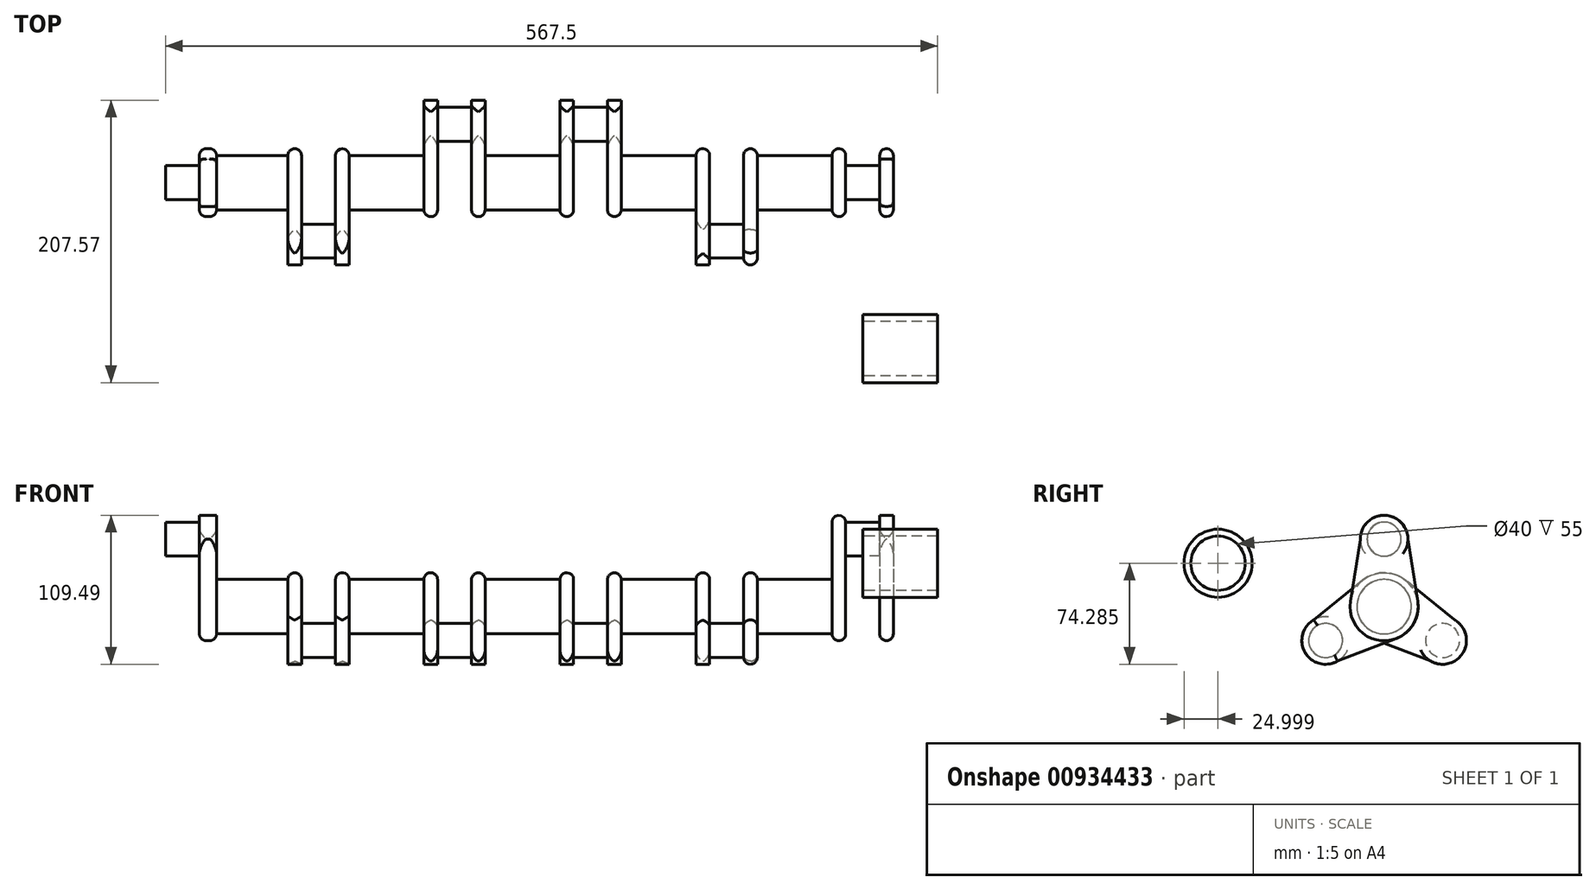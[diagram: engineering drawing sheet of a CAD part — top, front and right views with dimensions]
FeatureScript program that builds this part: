
annotation { "Feature Type Name" : "Feature", "Feature Type Description" : "" }
export const myFeature = defineFeature(function(context is Context, id is Id, definition is map)
    precondition{}
    {
        {
            var Q0;
            Q0=qCreatedBy(makeId("Right.planeOp"),FACE);
            cPlane(context, id + "F0", {"entities" : qUnion([Q0]), "cplaneType" : CPlaneType.OFFSET, "offset" : 100 * mm, "width" : 150 * mm, "height" : 150 * mm});
        }
        {
            var Q0;
            Q0=qCreatedBy(id+"F0.planeOp",FACE);
            cPlane(context, id + "F1", {"entities" : qUnion([Q0]), "cplaneType" : CPlaneType.OFFSET, "offset" : 100 * mm, "width" : 150 * mm, "height" : 150 * mm});
        }
        {
            var Q0;
            Q0=qCreatedBy(id+"F1.planeOp",FACE);
            cPlane(context, id + "F2", {"entities" : qUnion([Q0]), "cplaneType" : CPlaneType.OFFSET, "offset" : 100 * mm, "width" : 150 * mm, "height" : 150 * mm});
        }
        {
            var Q0;
            Q0=qCreatedBy(makeId("Right.planeOp"),FACE);
            cPlane(context, id + "F3", {"entities" : qUnion([Q0]), "cplaneType" : CPlaneType.OFFSET, "offset" : 100 * mm, "oppositeDirection" : true, "width" : 150 * mm, "height" : 150 * mm});
        }
        {
            var Q0;
            Q0=qCreatedBy(id+"F3.planeOp",FACE);
            cPlane(context, id + "F4", {"entities" : qUnion([Q0]), "cplaneType" : CPlaneType.OFFSET, "offset" : 100 * mm, "oppositeDirection" : true, "width" : 150 * mm, "height" : 150 * mm});
        }
        {
            var Q0;
            Q0=qCreatedBy(id+"F2.planeOp",FACE);
            var sketch = newSketch(context, id + "F5", { "sketchPlane" : qUnion([Q0])});
            skCircle(sketch, "E0", {"center": v(0, 0) * mm, "radius": 20 * mm});
            skCircle(sketch, "E1", {"center": v(0, 0) * mm, "radius": 49.66 * mm, "construction": true});
            skCircle(sketch, "E2", {"center": v(0, 49.66) * mm, "radius": 12.5 * mm});
            skLineSegment(sketch, "E3", {"start": v(0, 49.66) * mm, "end": v(0, 0) * mm, "construction": true});
            skLineSegment(sketch, "E4", {"start": v(43, -24.83) * mm, "end": v(0, 0) * mm, "construction": true});
            skSolve(sketch);
        }
        {
            var Q0;
            Q0=qCreatedBy(id+"F4.planeOp",FACE);
            var sketch = newSketch(context, id + "F6", { "sketchPlane" : qUnion([Q0])});
            skCircle(sketch, "E5", {"center": v(0, 0) * mm, "radius": 20 * mm});
            skCircle(sketch, "E6", {"center": v(0, 0) * mm, "radius": 49.66 * mm, "construction": true});
            skCircle(sketch, "E7", {"center": v(0, 49.66) * mm, "radius": 12.5 * mm});
            skLineSegment(sketch, "E8", {"start": v(0, 49.66) * mm, "end": v(0, 0) * mm, "construction": true});
            skLineSegment(sketch, "E9", {"start": v(43, -24.83) * mm, "end": v(0, 0) * mm, "construction": true});
            skSolve(sketch);
        }
        {
            var Q0;
            Q0=qCreatedBy(id+"F1.planeOp",FACE);
            var sketch = newSketch(context, id + "F7", { "sketchPlane" : qUnion([Q0])});
            skCircle(sketch, "E10", {"center": v(0, 0) * mm, "radius": 20 * mm});
            skCircle(sketch, "E11", {"center": v(0, 0) * mm, "radius": 49.66 * mm, "construction": true});
            skLineSegment(sketch, "E12", {"start": v(0, 49.66) * mm, "end": v(0, 0) * mm, "construction": true});
            skLineSegment(sketch, "E13", {"start": v(43, -24.83) * mm, "end": v(0, 0) * mm, "construction": true});
            skCircle(sketch, "E14.1.0", {"center": v(-43, -24.83) * mm, "radius": 12.5 * mm});
            skSolve(sketch);
        }
        {
            var Q0;
            Q0=qCreatedBy(id+"F3.planeOp",FACE);
            var sketch = newSketch(context, id + "F8", { "sketchPlane" : qUnion([Q0])});
            skCircle(sketch, "E15", {"center": v(0, 0) * mm, "radius": 20 * mm});
            skCircle(sketch, "E16", {"center": v(0, 0) * mm, "radius": 49.66 * mm, "construction": true});
            skLineSegment(sketch, "E17", {"start": v(0, 49.66) * mm, "end": v(0, 0) * mm, "construction": true});
            skLineSegment(sketch, "E18", {"start": v(43, -24.83) * mm, "end": v(0, 0) * mm, "construction": true});
            skCircle(sketch, "E19.1.0", {"center": v(-43, -24.83) * mm, "radius": 12.5 * mm});
            skSolve(sketch);
        }
        {
            var Q0;
            Q0=qCreatedBy(makeId("Right.planeOp"),FACE);
            var sketch = newSketch(context, id + "F9", { "sketchPlane" : qUnion([Q0])});
            skCircle(sketch, "E20", {"center": v(0, 0) * mm, "radius": 20 * mm});
            skCircle(sketch, "E21", {"center": v(0, 0) * mm, "radius": 49.66 * mm, "construction": true});
            skLineSegment(sketch, "E22", {"start": v(0, 49.66) * mm, "end": v(0, 0) * mm, "construction": true});
            skLineSegment(sketch, "E23", {"start": v(43, -24.83) * mm, "end": v(0, 0) * mm, "construction": true});
            skCircle(sketch, "E24", {"center": v(43, -24.83) * mm, "radius": 12.5 * mm});
            skSolve(sketch);
        }
        {
            var Q0;
            Q0=qCreatedBy(id+"F0.planeOp",FACE);
            var sketch = newSketch(context, id + "F10", { "sketchPlane" : qUnion([Q0])});
            skCircle(sketch, "E25", {"center": v(0, 0) * mm, "radius": 20 * mm});
            skCircle(sketch, "E26", {"center": v(0, 0) * mm, "radius": 49.66 * mm, "construction": true});
            skLineSegment(sketch, "E27", {"start": v(0, 49.66) * mm, "end": v(0, 0) * mm, "construction": true});
            skLineSegment(sketch, "E28", {"start": v(43, -24.83) * mm, "end": v(0, 0) * mm, "construction": true});
            skCircle(sketch, "E29", {"center": v(43, -24.83) * mm, "radius": 12.5 * mm});
            skSolve(sketch);
        }
        {
            var Q0;
            Q0=makeQuery(id+"F6.imprint","IMPRINT",FACE,{"disambiguationData":[TD([[makeQuery(id+"F6.imprint","IMPRINT",EDGE,{"derivedFrom":sQuery(id+"F6.wireOp",EDGE,"E7")}),1.0]])]});
            var Q1;
            Q1=makeQuery(id+"F8.imprint","IMPRINT",FACE,{"disambiguationData":[TD([[makeQuery(id+"F8.imprint","IMPRINT",EDGE,{"derivedFrom":sQuery(id+"F8.wireOp",EDGE,"E19.1.0")}),1.0]])]});
            var Q2;
            Q2=makeQuery(id+"F9.imprint","IMPRINT",FACE,{"disambiguationData":[TD([[makeQuery(id+"F9.imprint","IMPRINT",EDGE,{"derivedFrom":sQuery(id+"F9.wireOp",EDGE,"E24")}),1.0]])]});
            var Q3;
            Q3=makeQuery(id+"F10.imprint","IMPRINT",FACE,{"disambiguationData":[TD([[makeQuery(id+"F10.imprint","IMPRINT",EDGE,{"derivedFrom":sQuery(id+"F10.wireOp",EDGE,"E29")}),1.0]])]});
            var Q4;
            Q4=makeQuery(id+"F7.imprint","IMPRINT",FACE,{"disambiguationData":[TD([[makeQuery(id+"F7.imprint","IMPRINT",EDGE,{"derivedFrom":sQuery(id+"F7.wireOp",EDGE,"E14.1.0")}),1.0]])]});
            var Q5;
            Q5=makeQuery(id+"F5.imprint","IMPRINT",FACE,{"disambiguationData":[TD([[makeQuery(id+"F5.imprint","IMPRINT",EDGE,{"derivedFrom":sQuery(id+"F5.wireOp",EDGE,"E2")}),1.0]])]});
            extrude(context, id + "F11", {"entities" : qUnion([Q0, Q1, Q2, Q3, Q4, Q5]), "endBound" : BoundingType.SYMMETRIC, "depth" : 25 * mm, "offsetDistance" : 25 * mm});
        }
        {
            var Q0;
            Q0=makeQuery(id+"F11.opExtrude","CAP_FACE",FACE,{"disambiguationData":[OSD([sQuery(id+"F6.wireOp",EDGE,"E7")])],"isStart":false});
            var sketch = newSketch(context, id + "F12", { "sketchPlane" : qUnion([Q0])});
            skPoint(sketch, "E30.center.orphan", {"position": v(0, 49.66) * mm});
            skPoint(sketch, "E31.end.orphan", {"position": v(-12.5, 49.66) * mm});
            skArc(sketch, "E32", {"start": v(-24.7, 3.88) * mm, "mid": v(0, -25) * mm, "end": v(24.7, 3.88) * mm});
            skArc(sketch, "E33", {"start": v(17.5, 49.66) * mm, "mid": v(0, 67.16) * mm, "end": v(-17.5, 49.66) * mm});
            skLineSegment(sketch, "E34", {"start": v(-17.5, 49.66) * mm, "end": v(-24.7, 3.88) * mm});
            skLineSegment(sketch, "E35.MirrorCS", {"start": v(17.5, 49.66) * mm, "end": v(24.7, 3.88) * mm});
            skPoint(sketch, "E36.orphan", {"position": v(25.3, 0) * mm});
            skPoint(sketch, "E37.orphan", {"position": v(-25.3, 0) * mm});
            skSolve(sketch);
        }
        {
            var Q0;
            Q0 = qSketchRegion(id + "F12", true);
            extrude(context, id + "F13", {"entities" : qUnion([Q0]), "operationType" : NewBodyOperationType.ADD, "depth" : 12.5 * mm, "offsetDistance" : 25 * mm});
        }
        {
            var Q0;
            Q0=makeQuery(id+"F13.opExtrude","CAP_FACE",FACE,{"disambiguationData":[OSD([sQuery(id+"F12.wireOp",EDGE,"E32"),sQuery(id+"F12.wireOp",EDGE,"E33"),sQuery(id+"F12.wireOp",EDGE,"E34"),sQuery(id+"F12.wireOp",EDGE,"E35.MirrorCS")])],"isStart":false});
            var sketch = newSketch(context, id + "F14", { "sketchPlane" : qUnion([Q0])});
            skCircle(sketch, "E38", {"center": v(0, 0) * mm, "radius": 20 * mm});
            skSolve(sketch);
        }
        {
            var Q0;
            Q0 = qSketchRegion(id + "F14", true);
            extrude(context, id + "F15", {"entities" : qUnion([Q0]), "operationType" : NewBodyOperationType.ADD, "depth" : 53 * mm, "offsetDistance" : 25 * mm});
        }
        {
            var Q0;
            Q0=makeQuery(id+"F11.opExtrude","CAP_FACE",FACE,{"disambiguationData":[OSD([sQuery(id+"F8.wireOp",EDGE,"E19.1.0")])],"isStart":true});
            var sketch = newSketch(context, id + "F16", { "sketchPlane" : qUnion([Q0])});
            skPoint(sketch, "E39.center.orphan", {"position": v(43, -24.83) * mm});
            skPoint(sketch, "E40.end.orphan", {"position": v(49.25, -14) * mm});
            skArc(sketch, "E41", {"start": v(15.71, 19.45) * mm, "mid": v(-21.65, 12.5) * mm, "end": v(-8.99, -23.33) * mm});
            skArc(sketch, "E42", {"start": v(34.25, -39.98) * mm, "mid": v(58.16, -33.58) * mm, "end": v(51.75, -9.67) * mm});
            skLineSegment(sketch, "E43", {"start": v(51.75, -9.67) * mm, "end": v(15.71, 19.45) * mm});
            skLineSegment(sketch, "E44.MirrorCS", {"start": v(34.25, -39.98) * mm, "end": v(-8.99, -23.33) * mm});
            skPoint(sketch, "E45.orphan", {"position": v(-12.65, -21.92) * mm});
            skPoint(sketch, "E46.orphan", {"position": v(12.65, 21.92) * mm});
            skSolve(sketch);
        }
        {
            var Q0;
            Q0 = qSketchRegion(id + "F16", true);
            extrude(context, id + "F17", {"entities" : qUnion([Q0]), "operationType" : NewBodyOperationType.ADD, "depth" : 10 * mm, "offsetDistance" : 25 * mm});
        }
        {
            var Q0;
            Q0=makeQuery(id+"F11.opExtrude","CAP_FACE",FACE,{"disambiguationData":[OSD([sQuery(id+"F8.wireOp",EDGE,"E19.1.0")])],"isStart":false});
            var sketch = newSketch(context, id + "F18", { "sketchPlane" : qUnion([Q0])});
            skPoint(sketch, "E47.center.orphan", {"position": v(-43, -24.83) * mm});
            skPoint(sketch, "E48.end.orphan", {"position": v(-36.75, -35.65) * mm});
            skArc(sketch, "E49", {"start": v(8.99, -23.33) * mm, "mid": v(21.65, 12.5) * mm, "end": v(-15.71, 19.45) * mm});
            skArc(sketch, "E50", {"start": v(-51.75, -9.67) * mm, "mid": v(-58.16, -33.58) * mm, "end": v(-34.25, -39.98) * mm});
            skLineSegment(sketch, "E51", {"start": v(-34.25, -39.98) * mm, "end": v(8.99, -23.33) * mm});
            skLineSegment(sketch, "E52.MirrorCS", {"start": v(-51.75, -9.67) * mm, "end": v(-15.71, 19.45) * mm});
            skPoint(sketch, "E53.orphan", {"position": v(-12.65, 21.92) * mm});
            skPoint(sketch, "E54.orphan", {"position": v(12.65, -21.92) * mm});
            skSolve(sketch);
        }
        {
            var Q0;
            Q0 = qSketchRegion(id + "F18", true);
            extrude(context, id + "F19", {"entities" : qUnion([Q0]), "operationType" : NewBodyOperationType.ADD, "depth" : 10 * mm, "offsetDistance" : 25 * mm});
        }
        {
            var Q0;
            Q0=makeQuery(id+"F11.opExtrude","CAP_FACE",FACE,{"disambiguationData":[OSD([sQuery(id+"F9.wireOp",EDGE,"E24")])],"isStart":true});
            var sketch = newSketch(context, id + "F20", { "sketchPlane" : qUnion([Q0])});
            skPoint(sketch, "E55.center.orphan", {"position": v(-43, -24.83) * mm});
            skPoint(sketch, "E56.end.orphan", {"position": v(-36.75, -35.65) * mm});
            skArc(sketch, "E57", {"start": v(8.99, -23.33) * mm, "mid": v(21.65, 12.5) * mm, "end": v(-15.71, 19.45) * mm});
            skArc(sketch, "E58", {"start": v(-51.75, -9.67) * mm, "mid": v(-58.16, -33.58) * mm, "end": v(-34.25, -39.98) * mm});
            skLineSegment(sketch, "E59", {"start": v(-34.25, -39.98) * mm, "end": v(8.99, -23.33) * mm});
            skLineSegment(sketch, "E60.MirrorCS", {"start": v(-51.75, -9.67) * mm, "end": v(-15.71, 19.45) * mm});
            skPoint(sketch, "E61.orphan", {"position": v(-12.65, 21.92) * mm});
            skPoint(sketch, "E62.orphan", {"position": v(12.65, -21.92) * mm});
            skSolve(sketch);
        }
        {
            var Q0;
            Q0 = qSketchRegion(id + "F20", true);
            extrude(context, id + "F21", {"entities" : qUnion([Q0]), "operationType" : NewBodyOperationType.ADD, "depth" : 10 * mm, "offsetDistance" : 25 * mm});
        }
        {
            var Q0;
            Q0=makeQuery(id+"F11.opExtrude","CAP_FACE",FACE,{"disambiguationData":[OSD([sQuery(id+"F9.wireOp",EDGE,"E24")])],"isStart":false});
            var sketch = newSketch(context, id + "F22", { "sketchPlane" : qUnion([Q0])});
            skPoint(sketch, "E63.center.orphan", {"position": v(43, -24.83) * mm});
            skPoint(sketch, "E64.end.orphan", {"position": v(49.25, -14) * mm});
            skArc(sketch, "E65", {"start": v(15.71, 19.45) * mm, "mid": v(-21.65, 12.5) * mm, "end": v(-8.99, -23.33) * mm});
            skArc(sketch, "E66", {"start": v(34.25, -39.98) * mm, "mid": v(58.16, -33.58) * mm, "end": v(51.75, -9.67) * mm});
            skLineSegment(sketch, "E67", {"start": v(51.75, -9.67) * mm, "end": v(15.71, 19.45) * mm});
            skLineSegment(sketch, "E68.MirrorCS", {"start": v(34.25, -39.98) * mm, "end": v(-8.99, -23.33) * mm});
            skPoint(sketch, "E69.orphan", {"position": v(-12.65, -21.92) * mm});
            skPoint(sketch, "E70.orphan", {"position": v(12.65, 21.92) * mm});
            skSolve(sketch);
        }
        {
            var Q0;
            Q0 = qSketchRegion(id + "F22", true);
            extrude(context, id + "F23", {"entities" : qUnion([Q0]), "operationType" : NewBodyOperationType.ADD, "depth" : 10 * mm, "offsetDistance" : 25 * mm});
        }
        {
            var Q0;
            Q0=makeQuery(id+"F11.opExtrude","CAP_FACE",FACE,{"disambiguationData":[OSD([sQuery(id+"F10.wireOp",EDGE,"E29")])],"isStart":false});
            var sketch = newSketch(context, id + "F24", { "sketchPlane" : qUnion([Q0])});
            skPoint(sketch, "E71.center.orphan", {"position": v(43, -24.83) * mm});
            skPoint(sketch, "E72.end.orphan", {"position": v(49.25, -14) * mm});
            skArc(sketch, "E73", {"start": v(15.71, 19.45) * mm, "mid": v(-21.65, 12.5) * mm, "end": v(-8.99, -23.33) * mm});
            skArc(sketch, "E74", {"start": v(34.25, -39.98) * mm, "mid": v(58.16, -33.58) * mm, "end": v(51.75, -9.67) * mm});
            skLineSegment(sketch, "E75", {"start": v(51.75, -9.67) * mm, "end": v(15.71, 19.45) * mm});
            skLineSegment(sketch, "E76.MirrorCS", {"start": v(34.25, -39.98) * mm, "end": v(-8.99, -23.33) * mm});
            skPoint(sketch, "E77.orphan", {"position": v(-12.65, -21.92) * mm});
            skPoint(sketch, "E78.orphan", {"position": v(12.65, 21.92) * mm});
            skSolve(sketch);
        }
        {
            var Q0;
            Q0 = qSketchRegion(id + "F24", true);
            extrude(context, id + "F25", {"entities" : qUnion([Q0]), "operationType" : NewBodyOperationType.ADD, "depth" : 10 * mm, "offsetDistance" : 25 * mm});
        }
        {
            var Q0;
            Q0=makeQuery(id+"F11.opExtrude","CAP_FACE",FACE,{"disambiguationData":[OSD([sQuery(id+"F10.wireOp",EDGE,"E29")])],"isStart":true});
            var sketch = newSketch(context, id + "F26", { "sketchPlane" : qUnion([Q0])});
            skPoint(sketch, "E79.center.orphan", {"position": v(-43, -24.83) * mm});
            skPoint(sketch, "E80.end.orphan", {"position": v(-36.75, -35.65) * mm});
            skArc(sketch, "E81", {"start": v(8.99, -23.33) * mm, "mid": v(21.65, 12.5) * mm, "end": v(-15.71, 19.45) * mm});
            skArc(sketch, "E82", {"start": v(-51.75, -9.67) * mm, "mid": v(-58.16, -33.58) * mm, "end": v(-34.25, -39.98) * mm});
            skLineSegment(sketch, "E83", {"start": v(-34.25, -39.98) * mm, "end": v(8.99, -23.33) * mm});
            skLineSegment(sketch, "E84.MirrorCS", {"start": v(-51.75, -9.67) * mm, "end": v(-15.71, 19.45) * mm});
            skPoint(sketch, "E85.orphan", {"position": v(-12.65, 21.92) * mm});
            skPoint(sketch, "E86.orphan", {"position": v(12.65, -21.92) * mm});
            skSolve(sketch);
        }
        {
            var Q0;
            Q0 = qSketchRegion(id + "F26", true);
            extrude(context, id + "F27", {"entities" : qUnion([Q0]), "operationType" : NewBodyOperationType.ADD, "depth" : 10 * mm, "offsetDistance" : 25 * mm});
        }
        {
            var Q0;
            Q0=makeQuery(id+"F11.opExtrude","CAP_FACE",FACE,{"disambiguationData":[OSD([sQuery(id+"F7.wireOp",EDGE,"E14.1.0")])],"isStart":true});
            var sketch = newSketch(context, id + "F28", { "sketchPlane" : qUnion([Q0])});
            skPoint(sketch, "E87.center.orphan", {"position": v(43, -24.83) * mm});
            skPoint(sketch, "E88.end.orphan", {"position": v(49.25, -14) * mm});
            skArc(sketch, "E89", {"start": v(15.71, 19.45) * mm, "mid": v(-21.65, 12.5) * mm, "end": v(-8.99, -23.33) * mm});
            skArc(sketch, "E90", {"start": v(34.25, -39.98) * mm, "mid": v(58.16, -33.58) * mm, "end": v(51.75, -9.67) * mm});
            skLineSegment(sketch, "E91", {"start": v(51.75, -9.67) * mm, "end": v(15.71, 19.45) * mm});
            skLineSegment(sketch, "E92.MirrorCS", {"start": v(34.25, -39.98) * mm, "end": v(-8.99, -23.33) * mm});
            skPoint(sketch, "E93.orphan", {"position": v(-12.65, -21.92) * mm});
            skPoint(sketch, "E94.orphan", {"position": v(12.65, 21.92) * mm});
            skSolve(sketch);
        }
        {
            var Q0;
            Q0 = qSketchRegion(id + "F28", true);
            extrude(context, id + "F29", {"entities" : qUnion([Q0]), "operationType" : NewBodyOperationType.ADD, "depth" : 10 * mm, "offsetDistance" : 25 * mm});
        }
        {
            var Q0;
            Q0=makeQuery(id+"F11.opExtrude","CAP_FACE",FACE,{"disambiguationData":[OSD([sQuery(id+"F7.wireOp",EDGE,"E14.1.0")])],"isStart":false});
            var sketch = newSketch(context, id + "F30", { "sketchPlane" : qUnion([Q0])});
            skPoint(sketch, "E95.center.orphan", {"position": v(-43, -24.83) * mm});
            skPoint(sketch, "E96.end.orphan", {"position": v(-36.75, -35.65) * mm});
            skArc(sketch, "E97", {"start": v(8.99, -23.33) * mm, "mid": v(21.65, 12.5) * mm, "end": v(-15.71, 19.45) * mm});
            skArc(sketch, "E98", {"start": v(-51.75, -9.67) * mm, "mid": v(-58.16, -33.58) * mm, "end": v(-34.25, -39.98) * mm});
            skLineSegment(sketch, "E99", {"start": v(-34.25, -39.98) * mm, "end": v(8.99, -23.33) * mm});
            skLineSegment(sketch, "E100.MirrorCS", {"start": v(-51.75, -9.67) * mm, "end": v(-15.71, 19.45) * mm});
            skPoint(sketch, "E101.orphan", {"position": v(-12.65, 21.92) * mm});
            skPoint(sketch, "E102.orphan", {"position": v(12.65, -21.92) * mm});
            skSolve(sketch);
        }
        {
            var Q0;
            Q0=makeQuery(id+"F30.imprint","IMPRINT",FACE,{"disambiguationData":[TD([[makeQuery(id+"F30.imprint","IMPRINT",EDGE,{"derivedFrom":sQuery(id+"F30.wireOp",EDGE,"E97")}),1.0]])]});
            var Q1;
            Q1=makeQuery(id+"F30.imprint","IMPRINT",FACE,{"disambiguationData":[TD([[makeQuery(id+"F30.imprint","IMPRINT",EDGE,{"derivedFrom":makeQuery(id+"F11.opExtrude","CAP_EDGE",EDGE,{"disambiguationData":[OSD([sQuery(id+"F7.wireOp",EDGE,"E14.1.0")])],"isStart":false})}),1.0]])]});
            extrude(context, id + "F31", {"entities" : qUnion([Q0, Q1]), "operationType" : NewBodyOperationType.ADD, "depth" : 10 * mm, "offsetDistance" : 25 * mm});
        }
        {
            var Q0;
            Q0=makeQuery(id+"F11.opExtrude","CAP_FACE",FACE,{"disambiguationData":[OSD([sQuery(id+"F5.wireOp",EDGE,"E2")])],"isStart":false});
            var sketch = newSketch(context, id + "F32", { "sketchPlane" : qUnion([Q0])});
            skPoint(sketch, "E103.center.orphan", {"position": v(0, 49.66) * mm});
            skPoint(sketch, "E104.end.orphan", {"position": v(-12.5, 49.66) * mm});
            skArc(sketch, "E105", {"start": v(-24.7, 3.88) * mm, "mid": v(0, -25) * mm, "end": v(24.7, 3.88) * mm});
            skArc(sketch, "E106", {"start": v(17.5, 49.66) * mm, "mid": v(0, 67.16) * mm, "end": v(-17.5, 49.66) * mm});
            skLineSegment(sketch, "E107", {"start": v(-17.5, 49.66) * mm, "end": v(-24.7, 3.88) * mm});
            skLineSegment(sketch, "E108.MirrorCS", {"start": v(17.5, 49.66) * mm, "end": v(24.7, 3.88) * mm});
            skPoint(sketch, "E109.orphan", {"position": v(25.3, 0) * mm});
            skPoint(sketch, "E110.orphan", {"position": v(-25.3, 0) * mm});
            skSolve(sketch);
        }
        {
            var Q0;
            Q0 = qSketchRegion(id + "F32", true);
            extrude(context, id + "F33", {"entities" : qUnion([Q0]), "operationType" : NewBodyOperationType.ADD, "depth" : 10 * mm, "offsetDistance" : 25 * mm});
        }
        {
            var Q0;
            Q0=makeQuery(id+"F11.opExtrude","CAP_FACE",FACE,{"disambiguationData":[OSD([sQuery(id+"F5.wireOp",EDGE,"E2")])],"isStart":true});
            var sketch = newSketch(context, id + "F34", { "sketchPlane" : qUnion([Q0])});
            skPoint(sketch, "E111.center.orphan", {"position": v(0, 49.66) * mm});
            skPoint(sketch, "E112.end.orphan", {"position": v(-12.5, 49.66) * mm});
            skArc(sketch, "E113", {"start": v(-24.7, 3.88) * mm, "mid": v(0, -25) * mm, "end": v(24.7, 3.88) * mm});
            skArc(sketch, "E114", {"start": v(17.5, 49.66) * mm, "mid": v(0, 67.16) * mm, "end": v(-17.5, 49.66) * mm});
            skLineSegment(sketch, "E115", {"start": v(-17.5, 49.66) * mm, "end": v(-24.7, 3.88) * mm});
            skLineSegment(sketch, "E116.MirrorCS", {"start": v(17.5, 49.66) * mm, "end": v(24.7, 3.88) * mm});
            skPoint(sketch, "E117.orphan", {"position": v(25.3, 0) * mm});
            skPoint(sketch, "E118.orphan", {"position": v(-25.3, 0) * mm});
            skSolve(sketch);
        }
        {
            var Q0;
            Q0=makeQuery(id+"F19.opExtrude","CAP_FACE",FACE,{"disambiguationData":[OSD([sQuery(id+"F18.wireOp",EDGE,"E49"),sQuery(id+"F18.wireOp",EDGE,"E50"),sQuery(id+"F18.wireOp",EDGE,"E51"),sQuery(id+"F18.wireOp",EDGE,"E52.MirrorCS")])],"isStart":false});
            var sketch = newSketch(context, id + "F35", { "sketchPlane" : qUnion([Q0])});
            skCircle(sketch, "E119", {"center": v(0, 0) * mm, "radius": 20 * mm});
            skSolve(sketch);
        }
        {
            var Q0;
            Q0 = qSketchRegion(id + "F35", true);
            extrude(context, id + "F36", {"entities" : qUnion([Q0]), "operationType" : NewBodyOperationType.ADD, "depth" : 56 * mm, "offsetDistance" : 25 * mm});
        }
        {
            var Q0;
            Q0=makeQuery(id+"F23.opExtrude","CAP_FACE",FACE,{"disambiguationData":[OSD([sQuery(id+"F22.wireOp",EDGE,"E65"),sQuery(id+"F22.wireOp",EDGE,"E66"),sQuery(id+"F22.wireOp",EDGE,"E67"),sQuery(id+"F22.wireOp",EDGE,"E68.MirrorCS")])],"isStart":false});
            var sketch = newSketch(context, id + "F37", { "sketchPlane" : qUnion([Q0])});
            skCircle(sketch, "E120", {"center": v(0, 0) * mm, "radius": 20 * mm});
            skSolve(sketch);
        }
        {
            var Q0;
            Q0 = qSketchRegion(id + "F37", true);
            extrude(context, id + "F38", {"entities" : qUnion([Q0]), "operationType" : NewBodyOperationType.ADD, "depth" : 56 * mm, "offsetDistance" : 25 * mm});
        }
        {
            var Q0;
            Q0=makeQuery(id+"F25.opExtrude","CAP_FACE",FACE,{"disambiguationData":[OSD([sQuery(id+"F24.wireOp",EDGE,"E73"),sQuery(id+"F24.wireOp",EDGE,"E74"),sQuery(id+"F24.wireOp",EDGE,"E75"),sQuery(id+"F24.wireOp",EDGE,"E76.MirrorCS")])],"isStart":false});
            var sketch = newSketch(context, id + "F39", { "sketchPlane" : qUnion([Q0])});
            skCircle(sketch, "E121", {"center": v(0, 0) * mm, "radius": 20 * mm});
            skSolve(sketch);
        }
        {
            var Q0;
            Q0 = qSketchRegion(id + "F39", true);
            extrude(context, id + "F40", {"entities" : qUnion([Q0]), "operationType" : NewBodyOperationType.ADD, "depth" : 56 * mm, "offsetDistance" : 25 * mm});
        }
        {
            var Q0;
            Q0=makeQuery(id+"F34.imprint","IMPRINT",FACE,{"disambiguationData":[TD([[makeQuery(id+"F34.imprint","IMPRINT",EDGE,{"derivedFrom":sQuery(id+"F34.wireOp",EDGE,"E113")}),1.0]])]});
            var Q1;
            Q1=makeQuery(id+"F34.imprint","IMPRINT",FACE,{"disambiguationData":[TD([[makeQuery(id+"F34.imprint","IMPRINT",EDGE,{"derivedFrom":makeQuery(id+"F11.opExtrude","CAP_EDGE",EDGE,{"disambiguationData":[OSD([sQuery(id+"F5.wireOp",EDGE,"E2")])],"isStart":true})}),-1.0]])]});
            extrude(context, id + "F41", {"entities" : qUnion([Q0, Q1]), "operationType" : NewBodyOperationType.ADD, "depth" : 10 * mm, "offsetDistance" : 25 * mm});
        }
        {
            var Q0;
            Q0=makeQuery(id+"F31.opExtrude","CAP_FACE",FACE,{"disambiguationData":[OSD([sQuery(id+"F30.wireOp",EDGE,"E97"),sQuery(id+"F30.wireOp",EDGE,"E98"),sQuery(id+"F30.wireOp",EDGE,"E99"),sQuery(id+"F30.wireOp",EDGE,"E100.MirrorCS")])],"isStart":false});
            var sketch = newSketch(context, id + "F42", { "sketchPlane" : qUnion([Q0])});
            skCircle(sketch, "E122", {"center": v(0, 0) * mm, "radius": 20 * mm});
            skSolve(sketch);
        }
        {
            var Q0;
            Q0 = qSketchRegion(id + "F42", true);
            extrude(context, id + "F43", {"entities" : qUnion([Q0]), "operationType" : NewBodyOperationType.ADD, "depth" : 56 * mm, "offsetDistance" : 25 * mm});
        }
        {
            var Q0;
            Q0=makeQuery(id+"F41.opExtrude","CAP_EDGE",EDGE,{"disambiguationData":[OSD([sQuery(id+"F34.wireOp",EDGE,"E113")])],"isStart":false});
            var Q1;
            Q1=makeQuery(id+"F41.opExtrude","CAP_EDGE",EDGE,{"disambiguationData":[OSD([sQuery(id+"F34.wireOp",EDGE,"E113")])],"isStart":true});
            var Q2;
            Q2=makeQuery(id+"F41.opExtrude","SWEPT_FACE",FACE,{"disambiguationData":[OSD([sQuery(id+"F34.wireOp",EDGE,"E114")])]});
            var Q3;
            Q3=makeQuery(id+"F33.opExtrude","SWEPT_FACE",FACE,{"disambiguationData":[OSD([sQuery(id+"F32.wireOp",EDGE,"E107")])]});
            var Q4;
            Q4=makeQuery(id+"F33.opExtrude","CAP_EDGE",EDGE,{"disambiguationData":[OSD([sQuery(id+"F32.wireOp",EDGE,"E105")])],"isStart":true});
            var Q5;
            Q5=makeQuery(id+"F31.opExtrude","SWEPT_FACE",FACE,{"disambiguationData":[OSD([sQuery(id+"F30.wireOp",EDGE,"E97")])]});
            var Q6;
            Q6=makeQuery(id+"F31.opExtrude","CAP_EDGE",EDGE,{"disambiguationData":[OSD([sQuery(id+"F30.wireOp",EDGE,"E98")])],"isStart":true});
            var Q7;
            Q7=makeQuery(id+"F31.opExtrude","CAP_EDGE",EDGE,{"disambiguationData":[OSD([sQuery(id+"F30.wireOp",EDGE,"E98")])],"isStart":false});
            var Q8;
            Q8=makeQuery(id+"F29.opExtrude","SWEPT_FACE",FACE,{"disambiguationData":[OSD([sQuery(id+"F28.wireOp",EDGE,"E91")])]});
            var Q9;
            Q9=makeQuery(id+"F25.opExtrude","SWEPT_FACE",FACE,{"disambiguationData":[OSD([sQuery(id+"F24.wireOp",EDGE,"E75")])]});
            var Q10;
            Q10=makeQuery(id+"F27.opExtrude","SWEPT_FACE",FACE,{"disambiguationData":[OSD([sQuery(id+"F26.wireOp",EDGE,"E84.MirrorCS")])]});
            var Q11;
            Q11=makeQuery(id+"F23.opExtrude","SWEPT_FACE",FACE,{"disambiguationData":[OSD([sQuery(id+"F22.wireOp",EDGE,"E67")])]});
            var Q12;
            Q12=makeQuery(id+"F21.opExtrude","SWEPT_FACE",FACE,{"disambiguationData":[OSD([sQuery(id+"F20.wireOp",EDGE,"E60.MirrorCS")])]});
            var Q13;
            Q13=makeQuery(id+"F17.opExtrude","SWEPT_FACE",FACE,{"disambiguationData":[OSD([sQuery(id+"F16.wireOp",EDGE,"E44.MirrorCS")])]});
            var Q14;
            Q14=makeQuery(id+"F19.opExtrude","SWEPT_FACE",FACE,{"disambiguationData":[OSD([sQuery(id+"F18.wireOp",EDGE,"E51")])]});
            var Q15;
            Q15=makeQuery(id+"F13.opExtrude","SWEPT_FACE",FACE,{"disambiguationData":[OSD([sQuery(id+"F12.wireOp",EDGE,"E35.MirrorCS")])]});
            fillet(context, id + "F44", {"entities" : qUnion([Q0, Q1, Q2, Q3, Q4, Q5, Q6, Q7, Q8, Q9, Q10, Q11, Q12, Q13, Q14, Q15]), "radius" : 5 * mm, "tangentPropagation" : true, "allowEdgeOverflow" : false});
        }
        {
            var Q0;
            Q0=qCreatedBy(id+"F2.planeOp",FACE);
            var sketch = newSketch(context, id + "F45", { "sketchPlane" : qUnion([Q0])});
            skCircle(sketch, "E123", {"center": v(-122.07, 31.96) * mm, "radius": 25 * mm});
            skCircle(sketch, "E124", {"center": v(-122.07, 31.96) * mm, "radius": 20 * mm});
            skSolve(sketch);
        }
        {
            var Q0;
            Q0 = qSketchRegion(id + "F45", true);
            extrude(context, id + "F46", {"entities" : qUnion([Q0]), "depth" : 55 * mm, "offsetDistance" : 25 * mm});
        }
    });
